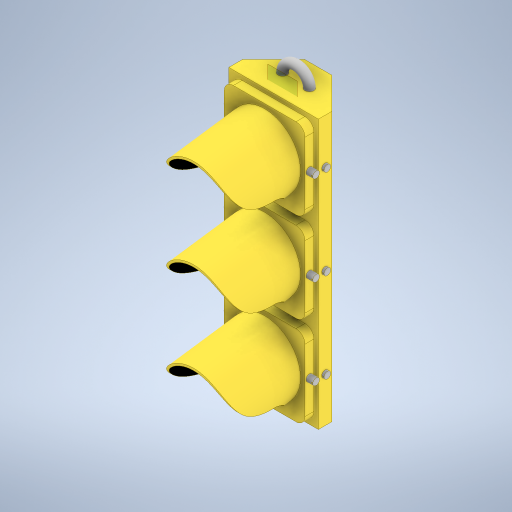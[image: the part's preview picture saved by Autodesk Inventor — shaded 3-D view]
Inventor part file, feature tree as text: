
AUTODESK INVENTOR PART (.ipt)
format: ipt  version: 2024 (Build 280153000, 153)  size: 630,784 bytes
history: native  units: in
note: dims shown in document units (in); Inventor stores cm internally (conversion verified against a paired STEP export)
features: sketch x14, extrude x7, projected_geometry x4, sweep x3, revolve x2, plane x1
ambient origin geometry x8: Origin, YZ Plane, XZ Plane, XY Plane, X Axis, Y Axis, Z Axis, Center Point
bodies: Solid1 (feature_tree)
feature tree (31):
  extrude  "Extrusion1"  Depth=30.0in
  sketch  "Sketch2"  dims[d2=10.0in d3=6.0in d4=0.0in]
  sketch  "Sketch3"  dims[d11=1.0in d12=1.0in]
  sketch  "Sketch5"  dims[d19=8.0in d20=7.5in]
  sketch  "Sketch4"  dims[d17=8.0in d18=7.5in]
  sweep  "Sweep1"
  sweep  "Sweep2"
  sweep  "Sweep3"
  extrude  "Extrusion2"  Depth=7.5in
  extrude  "Extrusion3"  Depth=7.5in
  extrude  "Extrusion4"  Depth=0.055in
  sketch  "Sketch9"  dims[d27=8.0in d28=0.055in]
  revolve  "Revolution1"  [1 undecoded]
  sketch  "Sketch11"  dims[d29=0.0in d30=0.0in d31=0.0in d32=0.0in]
  sketch  "Sketch12"  dims[d33=0.0in d34=0.0in d38=4.0in]
  revolve  "Revolution2"  [1 undecoded]
  sketch  "Sketch13"  dims[d39=30.5625in d40=0.0in d41=9.0in]
  extrude  "Extrusion5"  TaperAngle=0.0deg  [1 undecoded]
  extrude  "Extrusion6"  Depth=4.0in
  plane  "Work Plane2"
  extrude  "Extrusion7"  Depth=9.0in
  sketch  "Sketch1"  dims[d0=11.5in d1=30.0in]
  sketch  "Sketch6"  dims[d21=8.0in d22=7.5in]
  sketch  "Sketch7"  dims[d23=8.0in d24=0.055in]
  sketch  "Sketch8"  dims[d25=8.0in d26=0.055in]
  sketch  "Sketch14"  dims[d42=9.0in]
  sketch  "Sketch15"  dims[d43=9.0in d44=9.0in d45=1.0in d46=1.0in d47=0.0in d49=45.0deg d50=135.0deg d51=30.875in d52=0.0in d53=1.0in d54=1.0in d57=180.0deg d58=0.5in d59=0.5in d60=0.5in d61=0.5in d62=0.5in d63=0.5in d64=180.0deg d65=0.75in d66=0.75in d67=0.75in d68=0.75in d69=0.75in d70=0.75in d71=0.25in d72=0.0in d73=0.0in d74=0.0in d75=-4.0in d76=0.1in d77=0.1in d78=0.1in d79=10.0in d80=0.0in]
  projected_geometry  "Project Cut Edges1"
  projected_geometry  "Project Cut Edges2"
  projected_geometry  "Project Cut Edges3"
  projected_geometry  "Project Cut Edges4"
note: 3 required parameter values undecoded (feature->parameter linkage not recoverable at this tier; creation-order binding heuristic only, values carry confidence <= 0.55)